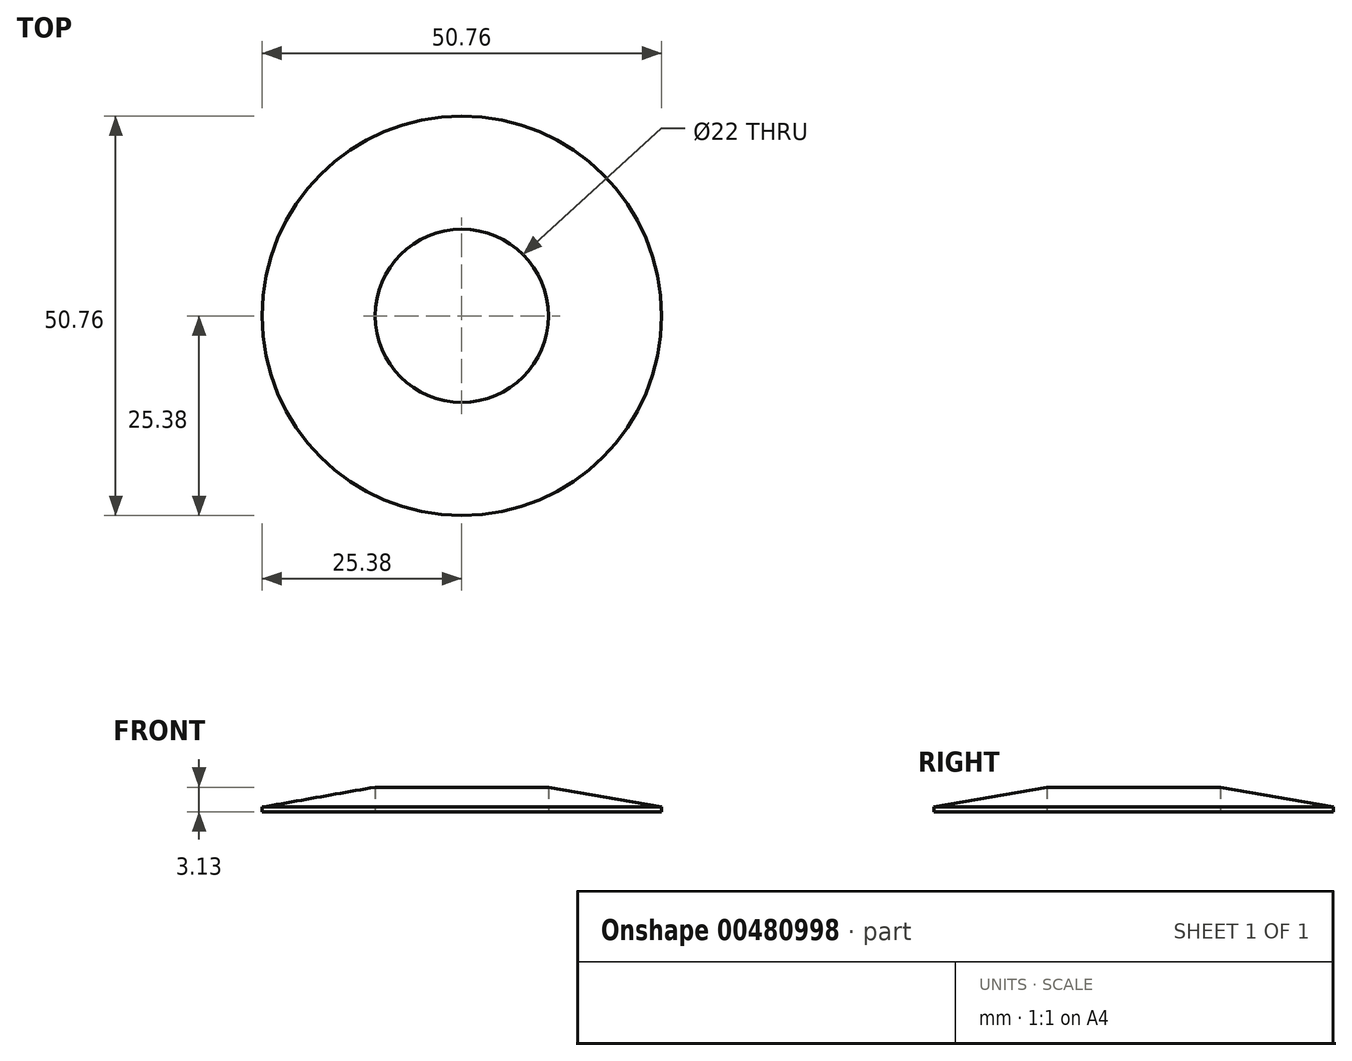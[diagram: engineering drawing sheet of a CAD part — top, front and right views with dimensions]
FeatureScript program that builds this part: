
annotation { "Feature Type Name" : "Feature", "Feature Type Description" : "" }
export const myFeature = defineFeature(function(context is Context, id is Id, definition is map)
    precondition{}
    {
        {
            var Q0;
            Q0=qCreatedBy(makeId("Right.planeOp"),FACE);
            var sketch = newSketch(context, id + "F0", { "sketchPlane" : qUnion([Q0])});
            skLineSegment(sketch, "E0", {"start": v(0, 0) * mm, "end": v(25.38, 0) * mm, "construction": true});
            skLineSegment(sketch, "E1", {"start": v(25.38, 0) * mm, "end": v(25.38, -3.2) * mm, "construction": true});
            skLineSegment(sketch, "E2", {"start": v(25.38, -3.2) * mm, "end": v(0, -3.2) * mm, "construction": true});
            skLineSegment(sketch, "E3.MirrorCS", {"start": v(0, 0) * mm, "end": v(-25.38, 0) * mm, "construction": true});
            skLineSegment(sketch, "E4.MirrorCS", {"start": v(-25.38, 0) * mm, "end": v(-25.38, -3.2) * mm, "construction": true});
            skLineSegment(sketch, "E5.MirrorCS", {"start": v(-25.38, -3.2) * mm, "end": v(0, -3.2) * mm, "construction": true});
            skLineSegment(sketch, "E6", {"start": v(11, 0) * mm, "end": v(11, -3.2) * mm, "construction": true});
            skLineSegment(sketch, "E7.MirrorCS", {"start": v(-11, 0) * mm, "end": v(-11, -3.2) * mm, "construction": true});
            skLineSegment(sketch, "E8", {"start": v(25.38, 0) * mm, "end": v(25.38, 0.6) * mm});
            skLineSegment(sketch, "E9", {"start": v(25.38, 0.6) * mm, "end": v(11, 3.13) * mm});
            skLineSegment(sketch, "E10", {"start": v(11, 3.13) * mm, "end": v(11, 0) * mm});
            skLineSegment(sketch, "E11", {"start": v(11, 0) * mm, "end": v(25.38, 0) * mm});
            skLineSegment(sketch, "E12", {"start": v(0, 0) * mm, "end": v(0, 8.24) * mm, "construction": true});
            skSolve(sketch);
        }
        {
            var Q0;
            Q0=makeQuery(id+"F0.imprint","IMPRINT",FACE,{"disambiguationData":[TD([[makeQuery(id+"F0.imprint","IMPRINT",EDGE,{"derivedFrom":sQuery(id+"F0.wireOp",EDGE,"E8")}),1.0]])]});
            var Q1;
            Q1=sQuery(id+"F0.wireOp",EDGE,"E12");
            revolve(context, id + "F1", {"entities" : qUnion([Q0]), "axis" : qUnion([Q1]), "revolveType" : RevolveType.FULL});
        }
    });
